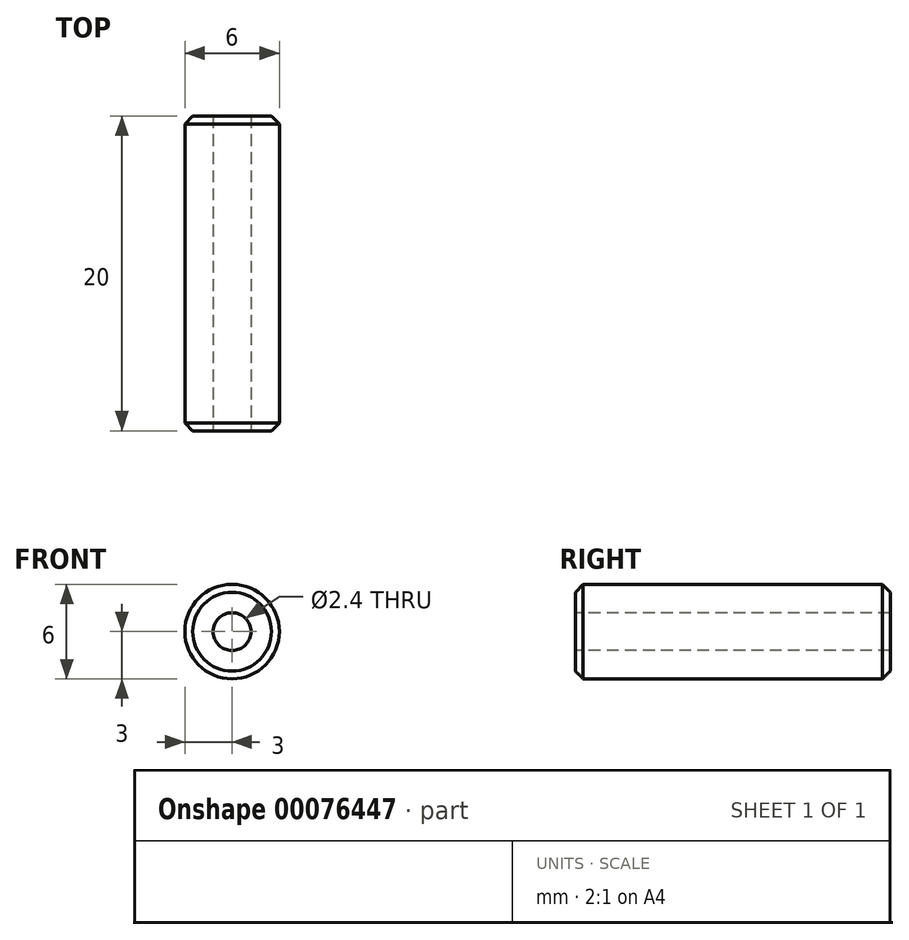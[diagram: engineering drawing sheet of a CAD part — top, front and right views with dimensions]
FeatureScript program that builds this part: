
annotation { "Feature Type Name" : "Feature", "Feature Type Description" : "" }
export const myFeature = defineFeature(function(context is Context, id is Id, definition is map)
    precondition{}
    {
        {
            var Q0;
            Q0=qCreatedBy(makeId("Front.planeOp"),FACE);
            var sketch = newSketch(context, id + "F0", { "sketchPlane" : qUnion([Q0])});
            skCircle(sketch, "E0", {"center": v(0, 0) * mm, "radius": 3 * mm});
            skSolve(sketch);
        }
        {
            var Q0;
            Q0=makeQuery(id+"F0.imprint","IMPRINT",FACE,{"disambiguationData":[TD([[makeQuery(id+"F0.imprint","IMPRINT",EDGE,{"derivedFrom":sQuery(id+"F0.wireOp",EDGE,"E0")}),1.0]])]});
            extrude(context, id + "F1", {"entities" : qUnion([Q0]), "oppositeDirection" : true, "depth" : 20 * mm});
        }
        {
            var Q0;
            Q0=sQuery(id+"F0.wireOp",VERTEX,"E0.center");
            var Q1;
            Q1=makeQuery(id+"F1.opExtrude","SWEPT_BODY",BODY,{"disambiguationData":[OSD([sQuery(id+"F0.wireOp",EDGE,"E0")])]});
            hole(context, id + "F2", {"style" : HoleStyle.SIMPLE, "endStyle" : HoleEndStyle.THROUGH, "standardTappedOrClearance" : lookupTablePath({ "standard" : "ISO", "engagement" : "75%", "pitch" : "0.6 mm", "size" : "M3", "type" : "Tapped" }), "standardBlindInLast" : lookupTablePath({ "standard" : "ISO", "engagement" : "75%", "pitch" : "0.6 mm", "size" : "M3", "type" : "Tapped" }), "holeDiameter" : 2.4 * mm, "locations" : qUnion([Q0]), "scope" : qUnion([Q1]), "isTappedThrough" : true, "showTappedDepth" : true});
        }
        {
            var Q0;
            Q0=makeQuery(id+"F1.opExtrude","CAP_EDGE",EDGE,{"disambiguationData":[OSD([sQuery(id+"F0.wireOp",EDGE,"E0")])],"isStart":true});
            var Q1;
            Q1=makeQuery(id+"F1.opExtrude","CAP_EDGE",EDGE,{"disambiguationData":[OSD([sQuery(id+"F0.wireOp",EDGE,"E0")])],"isStart":false});
            chamfer(context, id + "F3", {"entities" : qUnion([Q0, Q1]), "width" : .5 * mm, "tangentPropagation" : true});
        }
    });
